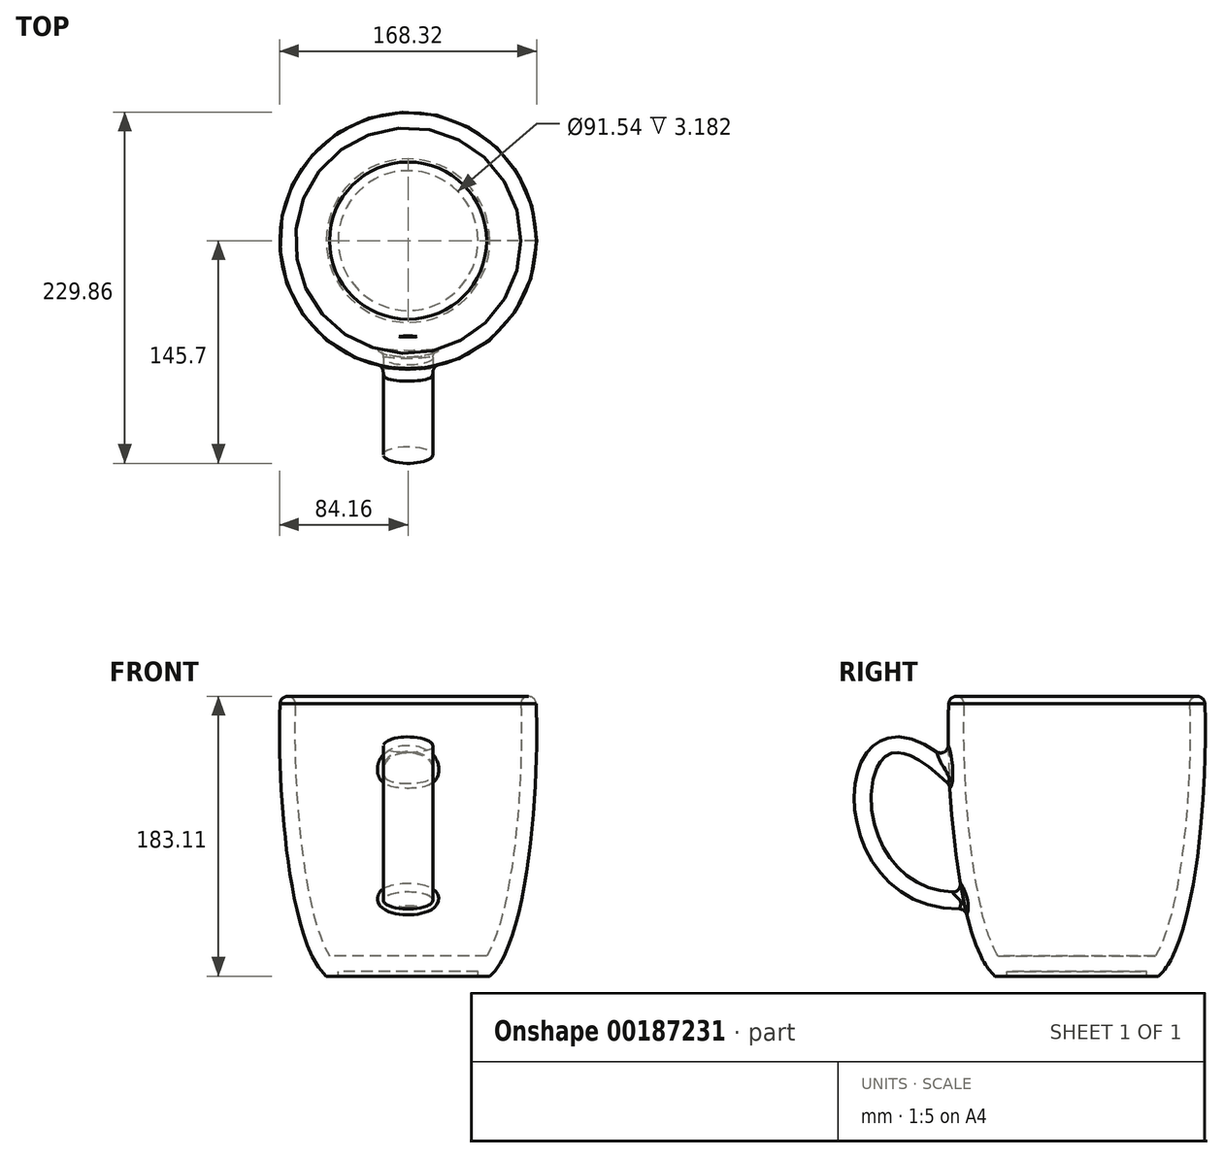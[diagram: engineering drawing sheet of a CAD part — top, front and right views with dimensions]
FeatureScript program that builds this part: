
annotation { "Feature Type Name" : "Feature", "Feature Type Description" : "" }
export const myFeature = defineFeature(function(context is Context, id is Id, definition is map)
    precondition{}
    {
        {
            var Q0;
            Q0=qCreatedBy(makeId("Front.planeOp"),FACE);
            var sketch = newSketch(context, id + "F0", { "sketchPlane" : qUnion([Q0])});
            skLineSegment(sketch, "E0", {"start": v(0, 144.72) * mm, "end": v(83.5, 144.72) * mm});
            skLineSegment(sketch, "E1", {"start": v(0, -35.2) * mm, "end": v(45.77, -35.2) * mm});
            skLineSegment(sketch, "E2", {"start": v(45.77, -35.2) * mm, "end": v(45.77, -38.39) * mm});
            skLineSegment(sketch, "E3", {"start": v(45.77, -38.39) * mm, "end": v(53.5, -38.39) * mm});
            skLineSegment(sketch, "E4", {"start": v(0, 144.72) * mm, "end": v(0, -35.2) * mm});
            skFitSpline(sketch, "E5", {"points": [v(83.5, 144.72) * mm, v(53.5, -38.39) * mm], "startDerivative": vector(8.22, -112.72) * mm, "endDerivative": vector(-83.19, -72.46) * mm});
            skSolve(sketch);
        }
        {
            var Q0;
            Q0=makeQuery(id+"F0.imprint","IMPRINT",FACE,{"disambiguationData":[TD([[makeQuery(id+"F0.imprint","IMPRINT",EDGE,{"derivedFrom":sQuery(id+"F0.wireOp",EDGE,"E0")}),-1.0]])]});
            var Q1;
            Q1=sQuery(id+"F0.wireOp",EDGE,"E4");
            revolve(context, id + "F1", {"entities" : qUnion([Q0]), "axis" : qUnion([Q1]), "revolveType" : RevolveType.FULL});
        }
        {
            var Q0;
            Q0=makeQuery(id+"F1.opRevolve","SWEPT_FACE",FACE,{"disambiguationData":[OSD([sQuery(id+"F0.wireOp",EDGE,"E0")])]});
            shell(context, id + "F2", {"entities" : qUnion([Q0]), "thickness" : 10 * mm});
        }
        {
            var Q0;
            Q0=qCreatedBy(makeId("Right.planeOp"),FACE);
            var sketch = newSketch(context, id + "F3", { "sketchPlane" : qUnion([Q0])});
            skFitSpline(sketch, "E6", {"points": [v(-79.93, 91.25) * mm, v(-68.08, 11.45) * mm], "startDerivative": vector(-235.97, 239.88) * mm, "endDerivative": vector(294.7, 34.34) * mm});
            skSolve(sketch);
        }
        {
            var Q0;
            Q0=qCreatedBy(makeId("Front.planeOp"),FACE);
            cPlane(context, id + "F4", {"entities" : qUnion([Q0]), "cplaneType" : CPlaneType.OFFSET, "offset" : 81 * mm, "width" : 150 * mm, "height" : 150 * mm});
        }
        {
            var Q0;
            Q0=qCreatedBy(id+"F4.planeOp",FACE);
            var sketch = newSketch(context, id + "F5", { "sketchPlane" : qUnion([Q0])});
            skEllipse(sketch, "E7", {"center": v(0, 91.85) * mm, "majorRadius": 16.28 * mm, "minorRadius": 7.76 * mm, "majorAxis": v(-1, 0)});
            skSolve(sketch);
        }
        {
            var Q0;
            Q0=makeQuery(id+"F5.imprint","IMPRINT",FACE,{"disambiguationData":[TD([[makeQuery(id+"F5.imprint","IMPRINT",EDGE,{"derivedFrom":sQuery(id+"F5.wireOp",EDGE,"E7")}),1.0]])]});
            var Q1;
            Q1=sQuery(id+"F3.wireOp",EDGE,"E6");
            sweep(context, id + "F6", {"operationType" : NewBodyOperationType.ADD, "profiles" : qUnion([Q0]), "path" : qUnion([Q1])});
        }
        {
            var Q0;
            Q0=makeQuery(id+"F1.opRevolve","SWEPT_EDGE",EDGE,{"disambiguationData":[OSD([sQuery(id+"F0.wireOp",EDGE,"E0"),sQuery(id+"F0.wireOp",EDGE,"E5")])]});
            var Q1;
            Q1=makeQuery(id+"F2.opShell","OFFSET_EDGE",EDGE,{"disambiguationData":[OSD([sQuery(id+"F0.wireOp",EDGE,"E0"),sQuery(id+"F0.wireOp",EDGE,"E5")])]});
            fillet(context, id + "F7", {"entities" : qUnion([Q0, Q1]), "radius" : 5 * mm, "tangentPropagation" : true, "allowEdgeOverflow" : false});
        }
        {
            var Q0;
            Q0=makeQuery(id+"F6.boolean.opBoolean","INTERSECT",EDGE,{"disambiguationData":[OD(0.0)],"derivedFrom":[makeQuery(id+"F1.opRevolve","SWEPT_FACE",FACE,{"disambiguationData":[OSD([sQuery(id+"F0.wireOp",EDGE,"E5")])]}),makeQuery(id+"F6.opSweep","SWEPT_FACE",FACE,{"disambiguationData":[OSD([sQuery(id+"F3.wireOp",EDGE,"E6"),sQuery(id+"F5.wireOp",EDGE,"E7")])]})]});
            var Q1;
            Q1=makeQuery(id+"F6.boolean.opBoolean","INTERSECT",EDGE,{"disambiguationData":[OD(1.0)],"derivedFrom":[makeQuery(id+"F1.opRevolve","SWEPT_FACE",FACE,{"disambiguationData":[OSD([sQuery(id+"F0.wireOp",EDGE,"E5")])]}),makeQuery(id+"F6.opSweep","SWEPT_FACE",FACE,{"disambiguationData":[OSD([sQuery(id+"F3.wireOp",EDGE,"E6"),sQuery(id+"F5.wireOp",EDGE,"E7")])]})]});
            fillet(context, id + "F8", {"entities" : qUnion([Q0, Q1]), "radius" : 5 * mm, "tangentPropagation" : true, "allowEdgeOverflow" : false});
        }
    });
